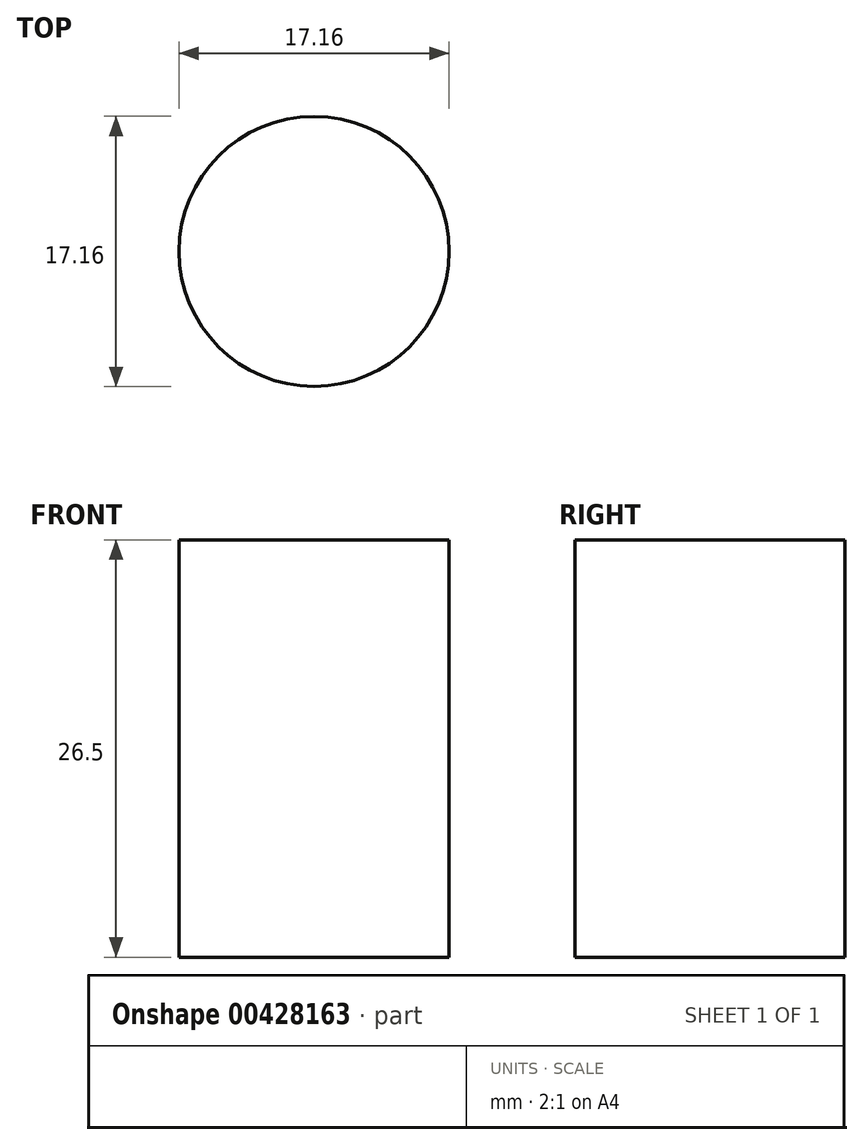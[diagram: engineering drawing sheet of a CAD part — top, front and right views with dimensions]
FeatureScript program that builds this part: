
annotation { "Feature Type Name" : "Feature", "Feature Type Description" : "" }
export const myFeature = defineFeature(function(context is Context, id is Id, definition is map)
    precondition{}
    {
        {
            var Q0;
            Q0=qCreatedBy(makeId("Top.planeOp"),FACE);
            var sketch = newSketch(context, id + "F0", { "sketchPlane" : qUnion([Q0])});
            skCircle(sketch, "E0", {"center": v(0, 0) * mm, "radius": 8.58 * mm});
            skSolve(sketch);
        }
        {
            var Q0;
            Q0 = qSketchRegion(id + "F0", true);
            extrude(context, id + "F1", {"entities" : qUnion([Q0]), "depth" : 26.5 * mm});
        }
    });
